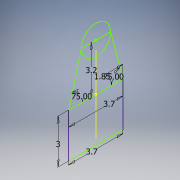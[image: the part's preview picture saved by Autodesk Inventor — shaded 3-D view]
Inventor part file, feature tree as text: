
AUTODESK INVENTOR PART (.ipt)
format: ipt  version: 2018 (Build 220112000, 112)  size: 95,232 bytes
history: native  units: in
note: dims shown in document units (in); Inventor stores cm internally (conversion verified against a paired STEP export)
features: sketch x1
ambient origin geometry x8: Origin, YZ Plane, XZ Plane, XY Plane, X Axis, Y Axis, Z Axis, Center Point
feature tree (1):
  sketch  "Sketch2"  dims[d0=145.6693in d1=72.8346in d2=75.0deg d3=75.0deg d4=125.9843in d5=145.6693in d6=118.1102in]
